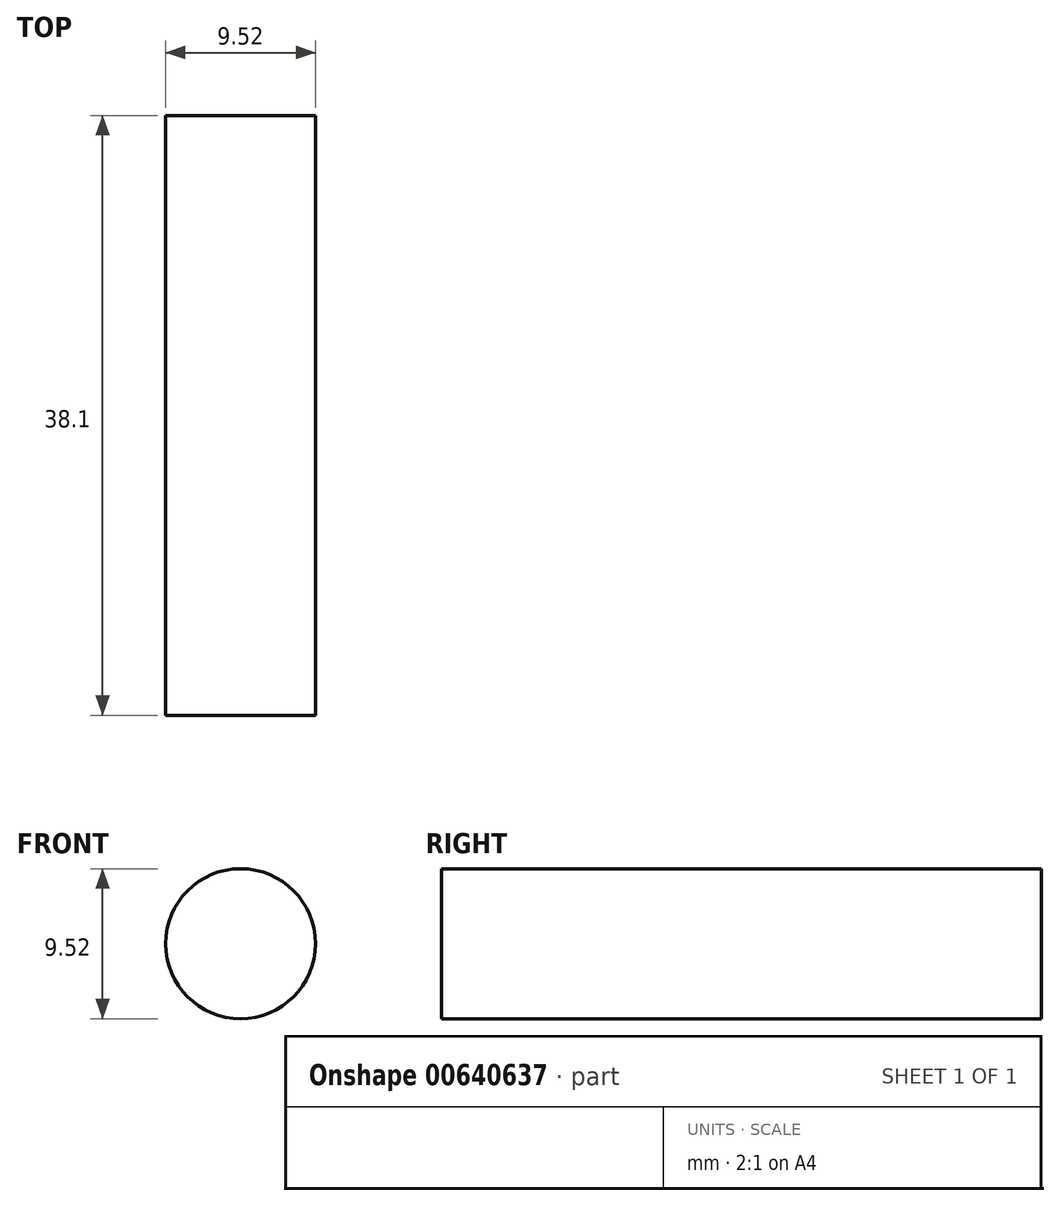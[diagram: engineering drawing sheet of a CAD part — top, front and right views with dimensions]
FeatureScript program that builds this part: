
annotation { "Feature Type Name" : "Feature", "Feature Type Description" : "" }
export const myFeature = defineFeature(function(context is Context, id is Id, definition is map)
    precondition{}
    {
        {
            var Q0;
            Q0=qCreatedBy(makeId("Front.planeOp"),FACE);
            var sketch = newSketch(context, id + "F0", { "sketchPlane" : qUnion([Q0])});
            skCircle(sketch, "E0", {"center": v(0, 0) * mm, "radius": 4.76 * mm});
            skSolve(sketch);
        }
        {
            var Q0;
            Q0=makeQuery(id+"F0.imprint","IMPRINT",FACE,{"disambiguationData":[TD([[makeQuery(id+"F0.imprint","IMPRINT",EDGE,{"derivedFrom":sQuery(id+"F0.wireOp",EDGE,"E0")}),1.0]])]});
            extrude(context, id + "F1", {"entities" : qUnion([Q0]), "depth" : 38.1 * mm, "offsetDistance" : 25.4 * mm});
        }
    });
